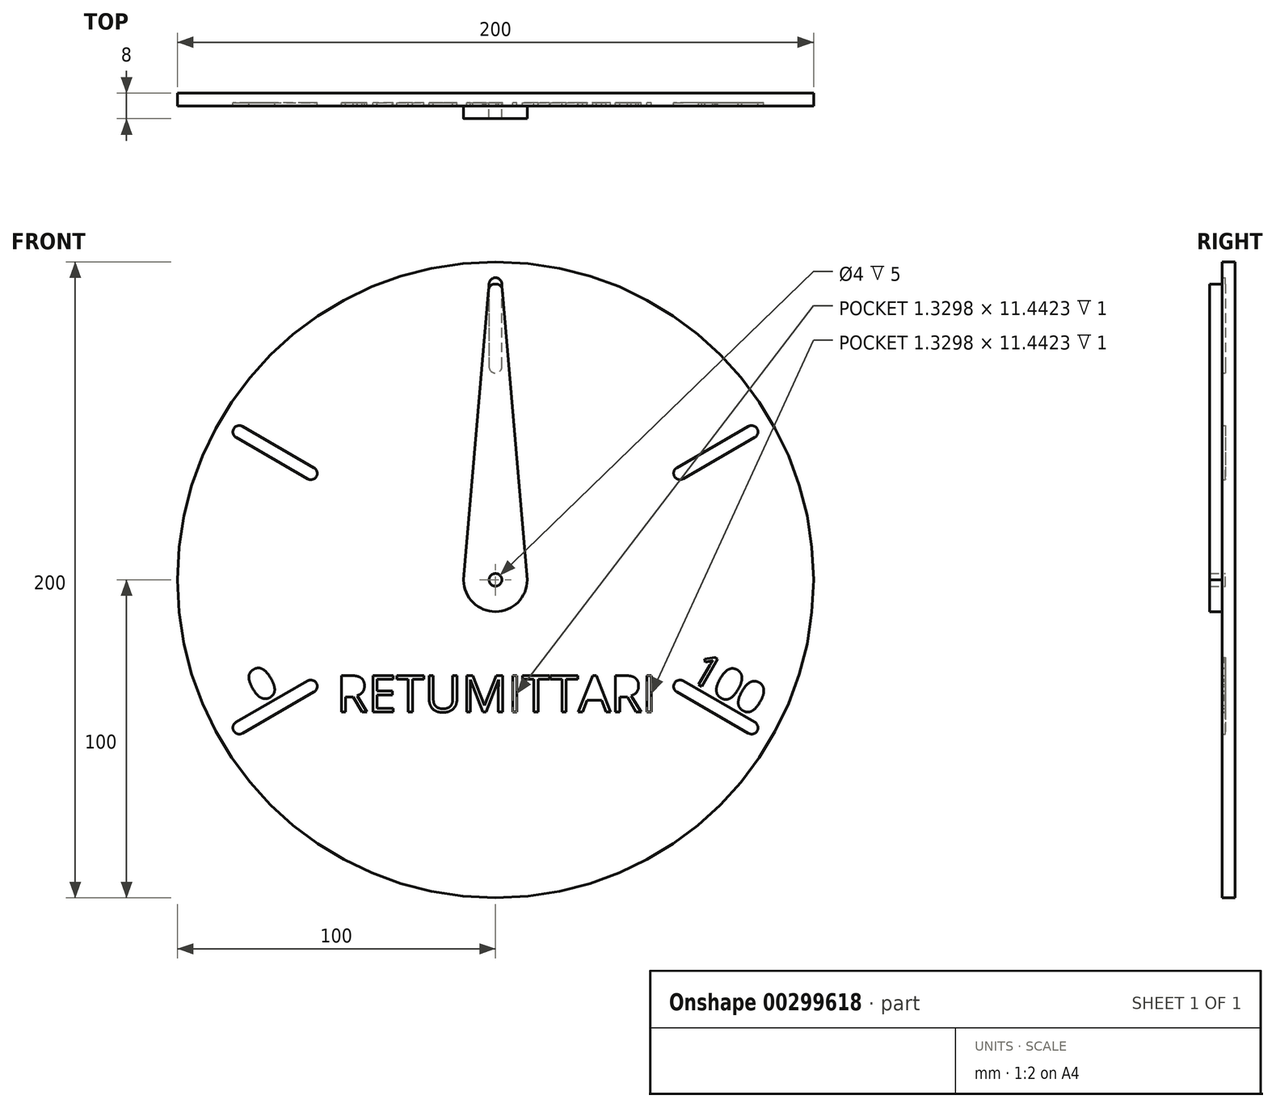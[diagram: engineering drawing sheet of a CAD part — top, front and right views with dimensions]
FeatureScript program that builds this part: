
annotation { "Feature Type Name" : "Feature", "Feature Type Description" : "" }
export const myFeature = defineFeature(function(context is Context, id is Id, definition is map)
    precondition{}
    {
        {
            var Q0;
            Q0=qCreatedBy(makeId("Front.planeOp"),FACE);
            var sketch = newSketch(context, id + "F0", { "sketchPlane" : qUnion([Q0])});
            skCircle(sketch, "E0", {"center": v(0, 0) * mm, "radius": 100 * mm});
            skCircle(sketch, "E1", {"center": v(0, 0) * mm, "radius": 2 * mm});
            skText(sketch, "E2", { "text": "RETUMITTARI", "fontName": "OpenSans-Regular.ttf"});
            skLineSegment(sketch, "E3", {"start": v(-79.54, -48.23) * mm, "end": v(-57.02, -35.23) * mm});
            skLineSegment(sketch, "E4", {"start": v(-59.02, -31.77) * mm, "end": v(-81.54, -44.77) * mm});
            skPoint(sketch, "E5.visualSharp", {"position": v(-81.27, -49.23) * mm});
            skArc(sketch, "E5.filletArc", {"start": v(-82.27, -47.5) * mm, "mid": v(-81.06, -48.43) * mm, "end": v(-79.54, -48.23) * mm});
            skPoint(sketch, "E6.visualSharp", {"position": v(-83.27, -45.77) * mm});
            skArc(sketch, "E6.filletArc", {"start": v(-81.54, -44.77) * mm, "mid": v(-82.47, -45.98) * mm, "end": v(-82.27, -47.5) * mm});
            skPoint(sketch, "E7.visualSharp", {"position": v(-57.3, -30.77) * mm});
            skArc(sketch, "E7.filletArc", {"start": v(-56.3, -32.5) * mm, "mid": v(-57.5, -31.57) * mm, "end": v(-59.02, -31.77) * mm});
            skPoint(sketch, "E8.visualSharp", {"position": v(-55.3, -34.23) * mm});
            skArc(sketch, "E8.filletArc", {"start": v(-57.02, -35.23) * mm, "mid": v(-56.1, -34.02) * mm, "end": v(-56.3, -32.5) * mm});
            skLineSegment(sketch, "E9.0", {"start": v(-57.3, -30.77) * mm, "end": v(-83.27, -45.77) * mm, "construction": true});
            skPoint(sketch, "E10.1.0", {"position": v(-55.3, 34.23) * mm});
            skLineSegment(sketch, "E10.1.1", {"start": v(-81.54, 44.77) * mm, "end": v(-59.02, 31.77) * mm});
            skPoint(sketch, "E10.1.2", {"position": v(-81.27, 49.23) * mm});
            skPoint(sketch, "E10.1.3", {"position": v(-57.3, 30.77) * mm});
            skLineSegment(sketch, "E10.1.4", {"start": v(-55.3, 34.23) * mm, "end": v(-81.27, 49.23) * mm, "construction": true});
            skLineSegment(sketch, "E10.1.5", {"start": v(-57.02, 35.23) * mm, "end": v(-79.54, 48.23) * mm});
            skArc(sketch, "E10.1.6", {"start": v(-56.3, 32.5) * mm, "mid": v(-56.1, 34.02) * mm, "end": v(-57.02, 35.23) * mm});
            skArc(sketch, "E10.1.7", {"start": v(-59.02, 31.77) * mm, "mid": v(-57.5, 31.57) * mm, "end": v(-56.3, 32.5) * mm});
            skArc(sketch, "E10.1.8", {"start": v(-79.54, 48.23) * mm, "mid": v(-81.06, 48.43) * mm, "end": v(-82.27, 47.5) * mm});
            skArc(sketch, "E10.1.9", {"start": v(-82.27, 47.5) * mm, "mid": v(-82.47, 45.98) * mm, "end": v(-81.54, 44.77) * mm});
            skPoint(sketch, "E10.1.10", {"position": v(-83.27, 45.77) * mm});
            skPoint(sketch, "E10.2.0", {"position": v(2, 65) * mm});
            skLineSegment(sketch, "E10.2.1", {"start": v(-2, 93) * mm, "end": v(-2, 67) * mm});
            skPoint(sketch, "E10.2.2", {"position": v(2, 95) * mm});
            skPoint(sketch, "E10.2.3", {"position": v(-2, 65) * mm});
            skLineSegment(sketch, "E10.2.4", {"start": v(2, 65) * mm, "end": v(2, 95) * mm, "construction": true});
            skLineSegment(sketch, "E10.2.5", {"start": v(2, 67) * mm, "end": v(2, 93) * mm});
            skArc(sketch, "E10.2.6", {"start": v(0, 65) * mm, "mid": v(1.41, 65.59) * mm, "end": v(2, 67) * mm});
            skArc(sketch, "E10.2.7", {"start": v(-2, 67) * mm, "mid": v(-1.41, 65.59) * mm, "end": v(0, 65) * mm});
            skArc(sketch, "E10.2.8", {"start": v(2, 93) * mm, "mid": v(1.41, 94.41) * mm, "end": v(0, 95) * mm});
            skArc(sketch, "E10.2.9", {"start": v(0, 95) * mm, "mid": v(-1.41, 94.41) * mm, "end": v(-2, 93) * mm});
            skPoint(sketch, "E10.2.10", {"position": v(-2, 95) * mm});
            skPoint(sketch, "E10.3.0", {"position": v(57.3, 30.77) * mm});
            skLineSegment(sketch, "E10.3.1", {"start": v(79.54, 48.23) * mm, "end": v(57.02, 35.23) * mm});
            skPoint(sketch, "E10.3.2", {"position": v(83.27, 45.77) * mm});
            skPoint(sketch, "E10.3.3", {"position": v(55.3, 34.23) * mm});
            skLineSegment(sketch, "E10.3.4", {"start": v(57.3, 30.77) * mm, "end": v(83.27, 45.77) * mm, "construction": true});
            skLineSegment(sketch, "E10.3.5", {"start": v(59.02, 31.77) * mm, "end": v(81.54, 44.77) * mm});
            skArc(sketch, "E10.3.6", {"start": v(56.3, 32.5) * mm, "mid": v(57.5, 31.57) * mm, "end": v(59.02, 31.77) * mm});
            skArc(sketch, "E10.3.7", {"start": v(57.02, 35.23) * mm, "mid": v(56.1, 34.02) * mm, "end": v(56.3, 32.5) * mm});
            skArc(sketch, "E10.3.8", {"start": v(81.54, 44.77) * mm, "mid": v(82.47, 45.98) * mm, "end": v(82.27, 47.5) * mm});
            skArc(sketch, "E10.3.9", {"start": v(82.27, 47.5) * mm, "mid": v(81.06, 48.43) * mm, "end": v(79.54, 48.23) * mm});
            skPoint(sketch, "E10.3.10", {"position": v(81.27, 49.23) * mm});
            skPoint(sketch, "E10.4.0", {"position": v(55.3, -34.23) * mm});
            skLineSegment(sketch, "E10.4.1", {"start": v(81.54, -44.77) * mm, "end": v(59.02, -31.77) * mm});
            skPoint(sketch, "E10.4.2", {"position": v(81.27, -49.23) * mm});
            skPoint(sketch, "E10.4.3", {"position": v(57.3, -30.77) * mm});
            skLineSegment(sketch, "E10.4.4", {"start": v(55.3, -34.23) * mm, "end": v(81.27, -49.23) * mm, "construction": true});
            skLineSegment(sketch, "E10.4.5", {"start": v(57.02, -35.23) * mm, "end": v(79.54, -48.23) * mm});
            skArc(sketch, "E10.4.6", {"start": v(56.3, -32.5) * mm, "mid": v(56.1, -34.02) * mm, "end": v(57.02, -35.23) * mm});
            skArc(sketch, "E10.4.7", {"start": v(59.02, -31.77) * mm, "mid": v(57.5, -31.57) * mm, "end": v(56.3, -32.5) * mm});
            skArc(sketch, "E10.4.8", {"start": v(79.54, -48.23) * mm, "mid": v(81.06, -48.43) * mm, "end": v(82.27, -47.5) * mm});
            skArc(sketch, "E10.4.9", {"start": v(82.27, -47.5) * mm, "mid": v(82.47, -45.98) * mm, "end": v(81.54, -44.77) * mm});
            skPoint(sketch, "E10.4.10", {"position": v(83.27, -45.77) * mm});
            skLineSegment(sketch, "E10.anchor1", {"start": v(0, 0) * mm, "end": v(-81.27, -49.23) * mm, "construction": true});
            skLineSegment(sketch, "E10.anchor2", {"start": v(0, 0) * mm, "end": v(83.27, -45.77) * mm, "construction": true});
            skText(sketch, "E11", { "text": "0\n", "fontName": "OpenSans-Regular.ttf"});
            skText(sketch, "E12", { "text": "100\n", "fontName": "OpenSans-Regular.ttf"});
            const initialGuessF0  = {"E2": [-0.05, -0.04154, 1, 0, 0.01154], "E11": [-0.07442, -0.03884, 0.86603, 0.5, 0.01], "E12": [0.06067, -0.03108, 0.86603, -0.5, 0.01]};
            skSetInitialGuess(sketch, initialGuessF0);
            skSolve(sketch);
        }
        {
            var Q0;
            Q0=makeQuery(id+"F0.imprint","IMPRINT",FACE,{"disambiguationData":[TD([[makeQuery(id+"F0.imprint","IMPRINT",EDGE,{"derivedFrom":sQuery(id+"F0.wireOp",EDGE,"E0")}),1.0]])]});
            extrude(context, id + "F1", {"entities" : qUnion([Q0]), "depth" : 1 * mm});
        }
        {
            var Q0;
            Q0=makeQuery(id+"F1.opExtrude","CAP_FACE",FACE,{"disambiguationData":[OSD([sQuery(id+"F0.wireOp",EDGE,"E0"),sQuery(id+"F0.wireOp",EDGE,"E1"),sQuery(id+"F0.wireOp",EDGE,"E2.sketch_text.stroke-0"),sQuery(id+"F0.wireOp",EDGE,"E2.sketch_text.stroke-1"),sQuery(id+"F0.wireOp",EDGE,"E2.sketch_text.stroke-2"),sQuery(id+"F0.wireOp",EDGE,"E2.sketch_text.stroke-3"),sQuery(id+"F0.wireOp",EDGE,"E2.sketch_text.stroke-4"),sQuery(id+"F0.wireOp",EDGE,"E2.sketch_text.stroke-5"),sQuery(id+"F0.wireOp",EDGE,"E2.sketch_text.stroke-6"),sQuery(id+"F0.wireOp",EDGE,"E2.sketch_text.stroke-7"),sQuery(id+"F0.wireOp",EDGE,"E2.sketch_text.stroke-8"),sQuery(id+"F0.wireOp",EDGE,"E2.sketch_text.stroke-9"),sQuery(id+"F0.wireOp",EDGE,"E2.sketch_text.stroke-10"),sQuery(id+"F0.wireOp",EDGE,"E2.sketch_text.stroke-18"),sQuery(id+"F0.wireOp",EDGE,"E2.sketch_text.stroke-19"),sQuery(id+"F0.wireOp",EDGE,"E2.sketch_text.stroke-20"),sQuery(id+"F0.wireOp",EDGE,"E2.sketch_text.stroke-21"),sQuery(id+"F0.wireOp",EDGE,"E2.sketch_text.stroke-22"),sQuery(id+"F0.wireOp",EDGE,"E2.sketch_text.stroke-23"),sQuery(id+"F0.wireOp",EDGE,"E2.sketch_text.stroke-24"),sQuery(id+"F0.wireOp",EDGE,"E2.sketch_text.stroke-25"),sQuery(id+"F0.wireOp",EDGE,"E2.sketch_text.stroke-26"),sQuery(id+"F0.wireOp",EDGE,"E2.sketch_text.stroke-27"),sQuery(id+"F0.wireOp",EDGE,"E2.sketch_text.stroke-28"),sQuery(id+"F0.wireOp",EDGE,"E2.sketch_text.stroke-29"),sQuery(id+"F0.wireOp",EDGE,"E2.sketch_text.stroke-30"),sQuery(id+"F0.wireOp",EDGE,"E2.sketch_text.stroke-31"),sQuery(id+"F0.wireOp",EDGE,"E2.sketch_text.stroke-32"),sQuery(id+"F0.wireOp",EDGE,"E2.sketch_text.stroke-33"),sQuery(id+"F0.wireOp",EDGE,"E2.sketch_text.stroke-34"),sQuery(id+"F0.wireOp",EDGE,"E2.sketch_text.stroke-35"),sQuery(id+"F0.wireOp",EDGE,"E2.sketch_text.stroke-36"),sQuery(id+"F0.wireOp",EDGE,"E2.sketch_text.stroke-37"),sQuery(id+"F0.wireOp",EDGE,"E2.sketch_text.stroke-38"),sQuery(id+"F0.wireOp",EDGE,"E2.sketch_text.stroke-39"),sQuery(id+"F0.wireOp",EDGE,"E2.sketch_text.stroke-40"),sQuery(id+"F0.wireOp",EDGE,"E2.sketch_text.stroke-41"),sQuery(id+"F0.wireOp",EDGE,"E2.sketch_text.stroke-42"),sQuery(id+"F0.wireOp",EDGE,"E2.sketch_text.stroke-43"),sQuery(id+"F0.wireOp",EDGE,"E2.sketch_text.stroke-44"),sQuery(id+"F0.wireOp",EDGE,"E2.sketch_text.stroke-45"),sQuery(id+"F0.wireOp",EDGE,"E2.sketch_text.stroke-46"),sQuery(id+"F0.wireOp",EDGE,"E2.sketch_text.stroke-47"),sQuery(id+"F0.wireOp",EDGE,"E2.sketch_text.stroke-48"),sQuery(id+"F0.wireOp",EDGE,"E2.sketch_text.stroke-49"),sQuery(id+"F0.wireOp",EDGE,"E2.sketch_text.stroke-50"),sQuery(id+"F0.wireOp",EDGE,"E2.sketch_text.stroke-51"),sQuery(id+"F0.wireOp",EDGE,"E2.sketch_text.stroke-52"),sQuery(id+"F0.wireOp",EDGE,"E2.sketch_text.stroke-53"),sQuery(id+"F0.wireOp",EDGE,"E2.sketch_text.stroke-54"),sQuery(id+"F0.wireOp",EDGE,"E2.sketch_text.stroke-55"),sQuery(id+"F0.wireOp",EDGE,"E2.sketch_text.stroke-56"),sQuery(id+"F0.wireOp",EDGE,"E2.sketch_text.stroke-57"),sQuery(id+"F0.wireOp",EDGE,"E2.sketch_text.stroke-58"),sQuery(id+"F0.wireOp",EDGE,"E2.sketch_text.stroke-59"),sQuery(id+"F0.wireOp",EDGE,"E2.sketch_text.stroke-60"),sQuery(id+"F0.wireOp",EDGE,"E2.sketch_text.stroke-61"),sQuery(id+"F0.wireOp",EDGE,"E2.sketch_text.stroke-62"),sQuery(id+"F0.wireOp",EDGE,"E2.sketch_text.stroke-63"),sQuery(id+"F0.wireOp",EDGE,"E2.sketch_text.stroke-64"),sQuery(id+"F0.wireOp",EDGE,"E2.sketch_text.stroke-65"),sQuery(id+"F0.wireOp",EDGE,"E2.sketch_text.stroke-66"),sQuery(id+"F0.wireOp",EDGE,"E2.sketch_text.stroke-67"),sQuery(id+"F0.wireOp",EDGE,"E2.sketch_text.stroke-68"),sQuery(id+"F0.wireOp",EDGE,"E2.sketch_text.stroke-69"),sQuery(id+"F0.wireOp",EDGE,"E2.sketch_text.stroke-70"),sQuery(id+"F0.wireOp",EDGE,"E2.sketch_text.stroke-71"),sQuery(id+"F0.wireOp",EDGE,"E2.sketch_text.stroke-72"),sQuery(id+"F0.wireOp",EDGE,"E2.sketch_text.stroke-73"),sQuery(id+"F0.wireOp",EDGE,"E2.sketch_text.stroke-74"),sQuery(id+"F0.wireOp",EDGE,"E2.sketch_text.stroke-75"),sQuery(id+"F0.wireOp",EDGE,"E2.sketch_text.stroke-76"),sQuery(id+"F0.wireOp",EDGE,"E2.sketch_text.stroke-77"),sQuery(id+"F0.wireOp",EDGE,"E2.sketch_text.stroke-78"),sQuery(id+"F0.wireOp",EDGE,"E2.sketch_text.stroke-79"),sQuery(id+"F0.wireOp",EDGE,"E2.sketch_text.stroke-80"),sQuery(id+"F0.wireOp",EDGE,"E2.sketch_text.stroke-81"),sQuery(id+"F0.wireOp",EDGE,"E2.sketch_text.stroke-82"),sQuery(id+"F0.wireOp",EDGE,"E2.sketch_text.stroke-83"),sQuery(id+"F0.wireOp",EDGE,"E2.sketch_text.stroke-84"),sQuery(id+"F0.wireOp",EDGE,"E2.sketch_text.stroke-85"),sQuery(id+"F0.wireOp",EDGE,"E2.sketch_text.stroke-86"),sQuery(id+"F0.wireOp",EDGE,"E2.sketch_text.stroke-87"),sQuery(id+"F0.wireOp",EDGE,"E2.sketch_text.stroke-88"),sQuery(id+"F0.wireOp",EDGE,"E2.sketch_text.stroke-89"),sQuery(id+"F0.wireOp",EDGE,"E2.sketch_text.stroke-90"),sQuery(id+"F0.wireOp",EDGE,"E2.sketch_text.stroke-91"),sQuery(id+"F0.wireOp",EDGE,"E2.sketch_text.stroke-92"),sQuery(id+"F0.wireOp",EDGE,"E2.sketch_text.stroke-93"),sQuery(id+"F0.wireOp",EDGE,"E2.sketch_text.stroke-94"),sQuery(id+"F0.wireOp",EDGE,"E2.sketch_text.stroke-95"),sQuery(id+"F0.wireOp",EDGE,"E2.sketch_text.stroke-96"),sQuery(id+"F0.wireOp",EDGE,"E2.sketch_text.stroke-97"),sQuery(id+"F0.wireOp",EDGE,"E2.sketch_text.stroke-103"),sQuery(id+"F0.wireOp",EDGE,"E2.sketch_text.stroke-104"),sQuery(id+"F0.wireOp",EDGE,"E2.sketch_text.stroke-105"),sQuery(id+"F0.wireOp",EDGE,"E2.sketch_text.stroke-106"),sQuery(id+"F0.wireOp",EDGE,"E2.sketch_text.stroke-107"),sQuery(id+"F0.wireOp",EDGE,"E2.sketch_text.stroke-108"),sQuery(id+"F0.wireOp",EDGE,"E2.sketch_text.stroke-109"),sQuery(id+"F0.wireOp",EDGE,"E2.sketch_text.stroke-110"),sQuery(id+"F0.wireOp",EDGE,"E2.sketch_text.stroke-111"),sQuery(id+"F0.wireOp",EDGE,"E2.sketch_text.stroke-112"),sQuery(id+"F0.wireOp",EDGE,"E2.sketch_text.stroke-113"),sQuery(id+"F0.wireOp",EDGE,"E2.sketch_text.stroke-121"),sQuery(id+"F0.wireOp",EDGE,"E2.sketch_text.stroke-122"),sQuery(id+"F0.wireOp",EDGE,"E2.sketch_text.stroke-123"),sQuery(id+"F0.wireOp",EDGE,"E2.sketch_text.stroke-124"),sQuery(id+"F0.wireOp",EDGE,"E3"),sQuery(id+"F0.wireOp",EDGE,"E4"),sQuery(id+"F0.wireOp",EDGE,"E5.filletArc"),sQuery(id+"F0.wireOp",EDGE,"E6.filletArc"),sQuery(id+"F0.wireOp",EDGE,"E7.filletArc"),sQuery(id+"F0.wireOp",EDGE,"E8.filletArc"),sQuery(id+"F0.wireOp",EDGE,"E10.1.1"),sQuery(id+"F0.wireOp",EDGE,"E10.1.5"),sQuery(id+"F0.wireOp",EDGE,"E10.1.6"),sQuery(id+"F0.wireOp",EDGE,"E10.1.7"),sQuery(id+"F0.wireOp",EDGE,"E10.1.8"),sQuery(id+"F0.wireOp",EDGE,"E10.1.9"),sQuery(id+"F0.wireOp",EDGE,"E10.2.1"),sQuery(id+"F0.wireOp",EDGE,"E10.2.5"),sQuery(id+"F0.wireOp",EDGE,"E10.2.6"),sQuery(id+"F0.wireOp",EDGE,"E10.2.7"),sQuery(id+"F0.wireOp",EDGE,"E10.2.8"),sQuery(id+"F0.wireOp",EDGE,"E10.2.9"),sQuery(id+"F0.wireOp",EDGE,"E10.3.1"),sQuery(id+"F0.wireOp",EDGE,"E10.3.5"),sQuery(id+"F0.wireOp",EDGE,"E10.3.6"),sQuery(id+"F0.wireOp",EDGE,"E10.3.7"),sQuery(id+"F0.wireOp",EDGE,"E10.3.8"),sQuery(id+"F0.wireOp",EDGE,"E10.3.9"),sQuery(id+"F0.wireOp",EDGE,"E10.4.1"),sQuery(id+"F0.wireOp",EDGE,"E10.4.5"),sQuery(id+"F0.wireOp",EDGE,"E10.4.6"),sQuery(id+"F0.wireOp",EDGE,"E10.4.7"),sQuery(id+"F0.wireOp",EDGE,"E10.4.8"),sQuery(id+"F0.wireOp",EDGE,"E10.4.9")])],"isStart":true});
            var sketch = newSketch(context, id + "F2", { "sketchPlane" : qUnion([Q0])});
            skCircle(sketch, "E13", {"center": v(0, 0) * mm, "radius": 100 * mm});
            skSolve(sketch);
        }
        {
            var Q0;
            Q0 = qSketchRegion(id + "F2", true);
            extrude(context, id + "F3", {"entities" : qUnion([Q0]), "operationType" : NewBodyOperationType.ADD, "depth" : 3 * mm});
        }
        {
            var Q0;
            Q0=makeQuery(id+"F1.opExtrude","CAP_FACE",FACE,{"disambiguationData":[OSD([sQuery(id+"F0.wireOp",EDGE,"E0"),sQuery(id+"F0.wireOp",EDGE,"E1"),sQuery(id+"F0.wireOp",EDGE,"E2.sketch_text.stroke-0"),sQuery(id+"F0.wireOp",EDGE,"E2.sketch_text.stroke-1"),sQuery(id+"F0.wireOp",EDGE,"E2.sketch_text.stroke-2"),sQuery(id+"F0.wireOp",EDGE,"E2.sketch_text.stroke-3"),sQuery(id+"F0.wireOp",EDGE,"E2.sketch_text.stroke-4"),sQuery(id+"F0.wireOp",EDGE,"E2.sketch_text.stroke-5"),sQuery(id+"F0.wireOp",EDGE,"E2.sketch_text.stroke-6"),sQuery(id+"F0.wireOp",EDGE,"E2.sketch_text.stroke-7"),sQuery(id+"F0.wireOp",EDGE,"E2.sketch_text.stroke-8"),sQuery(id+"F0.wireOp",EDGE,"E2.sketch_text.stroke-9"),sQuery(id+"F0.wireOp",EDGE,"E2.sketch_text.stroke-10"),sQuery(id+"F0.wireOp",EDGE,"E2.sketch_text.stroke-18"),sQuery(id+"F0.wireOp",EDGE,"E2.sketch_text.stroke-19"),sQuery(id+"F0.wireOp",EDGE,"E2.sketch_text.stroke-20"),sQuery(id+"F0.wireOp",EDGE,"E2.sketch_text.stroke-21"),sQuery(id+"F0.wireOp",EDGE,"E2.sketch_text.stroke-22"),sQuery(id+"F0.wireOp",EDGE,"E2.sketch_text.stroke-23"),sQuery(id+"F0.wireOp",EDGE,"E2.sketch_text.stroke-24"),sQuery(id+"F0.wireOp",EDGE,"E2.sketch_text.stroke-25"),sQuery(id+"F0.wireOp",EDGE,"E2.sketch_text.stroke-26"),sQuery(id+"F0.wireOp",EDGE,"E2.sketch_text.stroke-27"),sQuery(id+"F0.wireOp",EDGE,"E2.sketch_text.stroke-28"),sQuery(id+"F0.wireOp",EDGE,"E2.sketch_text.stroke-29"),sQuery(id+"F0.wireOp",EDGE,"E2.sketch_text.stroke-30"),sQuery(id+"F0.wireOp",EDGE,"E2.sketch_text.stroke-31"),sQuery(id+"F0.wireOp",EDGE,"E2.sketch_text.stroke-32"),sQuery(id+"F0.wireOp",EDGE,"E2.sketch_text.stroke-33"),sQuery(id+"F0.wireOp",EDGE,"E2.sketch_text.stroke-34"),sQuery(id+"F0.wireOp",EDGE,"E2.sketch_text.stroke-35"),sQuery(id+"F0.wireOp",EDGE,"E2.sketch_text.stroke-36"),sQuery(id+"F0.wireOp",EDGE,"E2.sketch_text.stroke-37"),sQuery(id+"F0.wireOp",EDGE,"E2.sketch_text.stroke-38"),sQuery(id+"F0.wireOp",EDGE,"E2.sketch_text.stroke-39"),sQuery(id+"F0.wireOp",EDGE,"E2.sketch_text.stroke-40"),sQuery(id+"F0.wireOp",EDGE,"E2.sketch_text.stroke-41"),sQuery(id+"F0.wireOp",EDGE,"E2.sketch_text.stroke-42"),sQuery(id+"F0.wireOp",EDGE,"E2.sketch_text.stroke-43"),sQuery(id+"F0.wireOp",EDGE,"E2.sketch_text.stroke-44"),sQuery(id+"F0.wireOp",EDGE,"E2.sketch_text.stroke-45"),sQuery(id+"F0.wireOp",EDGE,"E2.sketch_text.stroke-46"),sQuery(id+"F0.wireOp",EDGE,"E2.sketch_text.stroke-47"),sQuery(id+"F0.wireOp",EDGE,"E2.sketch_text.stroke-48"),sQuery(id+"F0.wireOp",EDGE,"E2.sketch_text.stroke-49"),sQuery(id+"F0.wireOp",EDGE,"E2.sketch_text.stroke-50"),sQuery(id+"F0.wireOp",EDGE,"E2.sketch_text.stroke-51"),sQuery(id+"F0.wireOp",EDGE,"E2.sketch_text.stroke-52"),sQuery(id+"F0.wireOp",EDGE,"E2.sketch_text.stroke-53"),sQuery(id+"F0.wireOp",EDGE,"E2.sketch_text.stroke-54"),sQuery(id+"F0.wireOp",EDGE,"E2.sketch_text.stroke-55"),sQuery(id+"F0.wireOp",EDGE,"E2.sketch_text.stroke-56"),sQuery(id+"F0.wireOp",EDGE,"E2.sketch_text.stroke-57"),sQuery(id+"F0.wireOp",EDGE,"E2.sketch_text.stroke-58"),sQuery(id+"F0.wireOp",EDGE,"E2.sketch_text.stroke-59"),sQuery(id+"F0.wireOp",EDGE,"E2.sketch_text.stroke-60"),sQuery(id+"F0.wireOp",EDGE,"E2.sketch_text.stroke-61"),sQuery(id+"F0.wireOp",EDGE,"E2.sketch_text.stroke-62"),sQuery(id+"F0.wireOp",EDGE,"E2.sketch_text.stroke-63"),sQuery(id+"F0.wireOp",EDGE,"E2.sketch_text.stroke-64"),sQuery(id+"F0.wireOp",EDGE,"E2.sketch_text.stroke-65"),sQuery(id+"F0.wireOp",EDGE,"E2.sketch_text.stroke-66"),sQuery(id+"F0.wireOp",EDGE,"E2.sketch_text.stroke-67"),sQuery(id+"F0.wireOp",EDGE,"E2.sketch_text.stroke-68"),sQuery(id+"F0.wireOp",EDGE,"E2.sketch_text.stroke-69"),sQuery(id+"F0.wireOp",EDGE,"E2.sketch_text.stroke-70"),sQuery(id+"F0.wireOp",EDGE,"E2.sketch_text.stroke-71"),sQuery(id+"F0.wireOp",EDGE,"E2.sketch_text.stroke-72"),sQuery(id+"F0.wireOp",EDGE,"E2.sketch_text.stroke-73"),sQuery(id+"F0.wireOp",EDGE,"E2.sketch_text.stroke-74"),sQuery(id+"F0.wireOp",EDGE,"E2.sketch_text.stroke-75"),sQuery(id+"F0.wireOp",EDGE,"E2.sketch_text.stroke-76"),sQuery(id+"F0.wireOp",EDGE,"E2.sketch_text.stroke-77"),sQuery(id+"F0.wireOp",EDGE,"E2.sketch_text.stroke-78"),sQuery(id+"F0.wireOp",EDGE,"E2.sketch_text.stroke-79"),sQuery(id+"F0.wireOp",EDGE,"E2.sketch_text.stroke-80"),sQuery(id+"F0.wireOp",EDGE,"E2.sketch_text.stroke-81"),sQuery(id+"F0.wireOp",EDGE,"E2.sketch_text.stroke-82"),sQuery(id+"F0.wireOp",EDGE,"E2.sketch_text.stroke-83"),sQuery(id+"F0.wireOp",EDGE,"E2.sketch_text.stroke-84"),sQuery(id+"F0.wireOp",EDGE,"E2.sketch_text.stroke-85"),sQuery(id+"F0.wireOp",EDGE,"E2.sketch_text.stroke-86"),sQuery(id+"F0.wireOp",EDGE,"E2.sketch_text.stroke-87"),sQuery(id+"F0.wireOp",EDGE,"E2.sketch_text.stroke-88"),sQuery(id+"F0.wireOp",EDGE,"E2.sketch_text.stroke-89"),sQuery(id+"F0.wireOp",EDGE,"E2.sketch_text.stroke-90"),sQuery(id+"F0.wireOp",EDGE,"E2.sketch_text.stroke-91"),sQuery(id+"F0.wireOp",EDGE,"E2.sketch_text.stroke-92"),sQuery(id+"F0.wireOp",EDGE,"E2.sketch_text.stroke-93"),sQuery(id+"F0.wireOp",EDGE,"E2.sketch_text.stroke-94"),sQuery(id+"F0.wireOp",EDGE,"E2.sketch_text.stroke-95"),sQuery(id+"F0.wireOp",EDGE,"E2.sketch_text.stroke-96"),sQuery(id+"F0.wireOp",EDGE,"E2.sketch_text.stroke-97"),sQuery(id+"F0.wireOp",EDGE,"E2.sketch_text.stroke-103"),sQuery(id+"F0.wireOp",EDGE,"E2.sketch_text.stroke-104"),sQuery(id+"F0.wireOp",EDGE,"E2.sketch_text.stroke-105"),sQuery(id+"F0.wireOp",EDGE,"E2.sketch_text.stroke-106"),sQuery(id+"F0.wireOp",EDGE,"E2.sketch_text.stroke-107"),sQuery(id+"F0.wireOp",EDGE,"E2.sketch_text.stroke-108"),sQuery(id+"F0.wireOp",EDGE,"E2.sketch_text.stroke-109"),sQuery(id+"F0.wireOp",EDGE,"E2.sketch_text.stroke-110"),sQuery(id+"F0.wireOp",EDGE,"E2.sketch_text.stroke-111"),sQuery(id+"F0.wireOp",EDGE,"E2.sketch_text.stroke-112"),sQuery(id+"F0.wireOp",EDGE,"E2.sketch_text.stroke-113"),sQuery(id+"F0.wireOp",EDGE,"E2.sketch_text.stroke-121"),sQuery(id+"F0.wireOp",EDGE,"E2.sketch_text.stroke-122"),sQuery(id+"F0.wireOp",EDGE,"E2.sketch_text.stroke-123"),sQuery(id+"F0.wireOp",EDGE,"E2.sketch_text.stroke-124"),sQuery(id+"F0.wireOp",EDGE,"E3"),sQuery(id+"F0.wireOp",EDGE,"E4"),sQuery(id+"F0.wireOp",EDGE,"E5.filletArc"),sQuery(id+"F0.wireOp",EDGE,"E6.filletArc"),sQuery(id+"F0.wireOp",EDGE,"E7.filletArc"),sQuery(id+"F0.wireOp",EDGE,"E8.filletArc"),sQuery(id+"F0.wireOp",EDGE,"E10.1.1"),sQuery(id+"F0.wireOp",EDGE,"E10.1.5"),sQuery(id+"F0.wireOp",EDGE,"E10.1.6"),sQuery(id+"F0.wireOp",EDGE,"E10.1.7"),sQuery(id+"F0.wireOp",EDGE,"E10.1.8"),sQuery(id+"F0.wireOp",EDGE,"E10.1.9"),sQuery(id+"F0.wireOp",EDGE,"E10.2.1"),sQuery(id+"F0.wireOp",EDGE,"E10.2.5"),sQuery(id+"F0.wireOp",EDGE,"E10.2.6"),sQuery(id+"F0.wireOp",EDGE,"E10.2.7"),sQuery(id+"F0.wireOp",EDGE,"E10.2.8"),sQuery(id+"F0.wireOp",EDGE,"E10.2.9"),sQuery(id+"F0.wireOp",EDGE,"E10.3.1"),sQuery(id+"F0.wireOp",EDGE,"E10.3.5"),sQuery(id+"F0.wireOp",EDGE,"E10.3.6"),sQuery(id+"F0.wireOp",EDGE,"E10.3.7"),sQuery(id+"F0.wireOp",EDGE,"E10.3.8"),sQuery(id+"F0.wireOp",EDGE,"E10.3.9"),sQuery(id+"F0.wireOp",EDGE,"E10.4.1"),sQuery(id+"F0.wireOp",EDGE,"E10.4.5"),sQuery(id+"F0.wireOp",EDGE,"E10.4.6"),sQuery(id+"F0.wireOp",EDGE,"E10.4.7"),sQuery(id+"F0.wireOp",EDGE,"E10.4.8"),sQuery(id+"F0.wireOp",EDGE,"E10.4.9"),sQuery(id+"F0.wireOp",EDGE,"E11.sketch_text.stroke-0"),sQuery(id+"F0.wireOp",EDGE,"E11.sketch_text.stroke-1"),sQuery(id+"F0.wireOp",EDGE,"E11.sketch_text.stroke-2"),sQuery(id+"F0.wireOp",EDGE,"E11.sketch_text.stroke-3"),sQuery(id+"F0.wireOp",EDGE,"E11.sketch_text.stroke-4"),sQuery(id+"F0.wireOp",EDGE,"E11.sketch_text.stroke-5"),sQuery(id+"F0.wireOp",EDGE,"E11.sketch_text.stroke-6"),sQuery(id+"F0.wireOp",EDGE,"E11.sketch_text.stroke-7"),sQuery(id+"F0.wireOp",EDGE,"E12.sketch_text.stroke-0"),sQuery(id+"F0.wireOp",EDGE,"E12.sketch_text.stroke-1"),sQuery(id+"F0.wireOp",EDGE,"E12.sketch_text.stroke-2"),sQuery(id+"F0.wireOp",EDGE,"E12.sketch_text.stroke-3"),sQuery(id+"F0.wireOp",EDGE,"E12.sketch_text.stroke-4"),sQuery(id+"F0.wireOp",EDGE,"E12.sketch_text.stroke-5"),sQuery(id+"F0.wireOp",EDGE,"E12.sketch_text.stroke-6"),sQuery(id+"F0.wireOp",EDGE,"E12.sketch_text.stroke-7"),sQuery(id+"F0.wireOp",EDGE,"E12.sketch_text.stroke-8"),sQuery(id+"F0.wireOp",EDGE,"E12.sketch_text.stroke-9"),sQuery(id+"F0.wireOp",EDGE,"E12.sketch_text.stroke-10"),sQuery(id+"F0.wireOp",EDGE,"E12.sketch_text.stroke-11"),sQuery(id+"F0.wireOp",EDGE,"E12.sketch_text.stroke-12"),sQuery(id+"F0.wireOp",EDGE,"E12.sketch_text.stroke-13"),sQuery(id+"F0.wireOp",EDGE,"E12.sketch_text.stroke-14"),sQuery(id+"F0.wireOp",EDGE,"E12.sketch_text.stroke-15"),sQuery(id+"F0.wireOp",EDGE,"E12.sketch_text.stroke-16"),sQuery(id+"F0.wireOp",EDGE,"E12.sketch_text.stroke-25"),sQuery(id+"F0.wireOp",EDGE,"E12.sketch_text.stroke-26"),sQuery(id+"F0.wireOp",EDGE,"E12.sketch_text.stroke-27"),sQuery(id+"F0.wireOp",EDGE,"E12.sketch_text.stroke-28"),sQuery(id+"F0.wireOp",EDGE,"E12.sketch_text.stroke-29"),sQuery(id+"F0.wireOp",EDGE,"E12.sketch_text.stroke-30"),sQuery(id+"F0.wireOp",EDGE,"E12.sketch_text.stroke-31"),sQuery(id+"F0.wireOp",EDGE,"E12.sketch_text.stroke-32")])],"isStart":false});
            var sketch = newSketch(context, id + "F4", { "sketchPlane" : qUnion([Q0])});
            skArc(sketch, "E14", {"start": v(-10, -0.1) * mm, "mid": v(0.05, -10) * mm, "end": v(10, 0) * mm});
            skLineSegment(sketch, "E15", {"start": v(-10, 0.1) * mm, "end": v(-2.16, 91.17) * mm});
            skLineSegment(sketch, "E16", {"start": v(-0.16, 93) * mm, "end": v(0.16, 93) * mm});
            skLineSegment(sketch, "E17", {"start": v(2.16, 91.17) * mm, "end": v(10, 0) * mm});
            skPoint(sketch, "E18.visualSharp", {"position": v(-2, 93) * mm});
            skArc(sketch, "E18.filletArc", {"start": v(-0.16, 93) * mm, "mid": v(-1.52, 92.47) * mm, "end": v(-2.16, 91.17) * mm});
            skPoint(sketch, "E19.visualSharp", {"position": v(2, 93) * mm});
            skArc(sketch, "E19.filletArc", {"start": v(2.16, 91.17) * mm, "mid": v(1.52, 92.47) * mm, "end": v(0.16, 93) * mm});
            skPoint(sketch, "E20.visualSharp", {"position": v(-10, 0) * mm});
            skArc(sketch, "E20.filletArc", {"start": v(-10, 0.1) * mm, "mid": v(-10, 0) * mm, "end": v(-10, -0.1) * mm});
            skCircle(sketch, "E21", {"center": v(0, 0) * mm, "radius": 2 * mm});
            skSolve(sketch);
        }
        {
            var Q0;
            Q0 = qSketchRegion(id + "F4", true);
            extrude(context, id + "F5", {"entities" : qUnion([Q0]), "operationType" : NewBodyOperationType.ADD, "depth" : 4 * mm});
        }
    });
